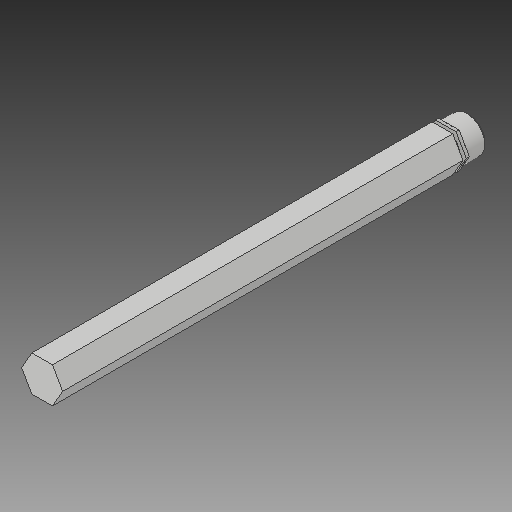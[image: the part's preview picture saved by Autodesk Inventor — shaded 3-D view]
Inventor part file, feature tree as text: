
AUTODESK INVENTOR PART (.ipt)
format: ipt  version: 2017 (Build 210142000, 142)  size: 88,576 bytes
history: native  units: in
note: dims shown in document units (in); Inventor stores cm internally (conversion verified against a paired STEP export)
features: chamfer x1
ambient origin geometry x8: Origin, YZ Plane, XZ Plane, XY Plane, X Axis, Y Axis, Z Axis, Center Point
bodies: Solid1 (feature_tree)
feature tree (1):
  chamfer  "Chamfer1"  [1 undecoded]
note: 1 required parameter value undecoded (feature->parameter linkage not recoverable at this tier; creation-order binding heuristic only, values carry confidence <= 0.55)
